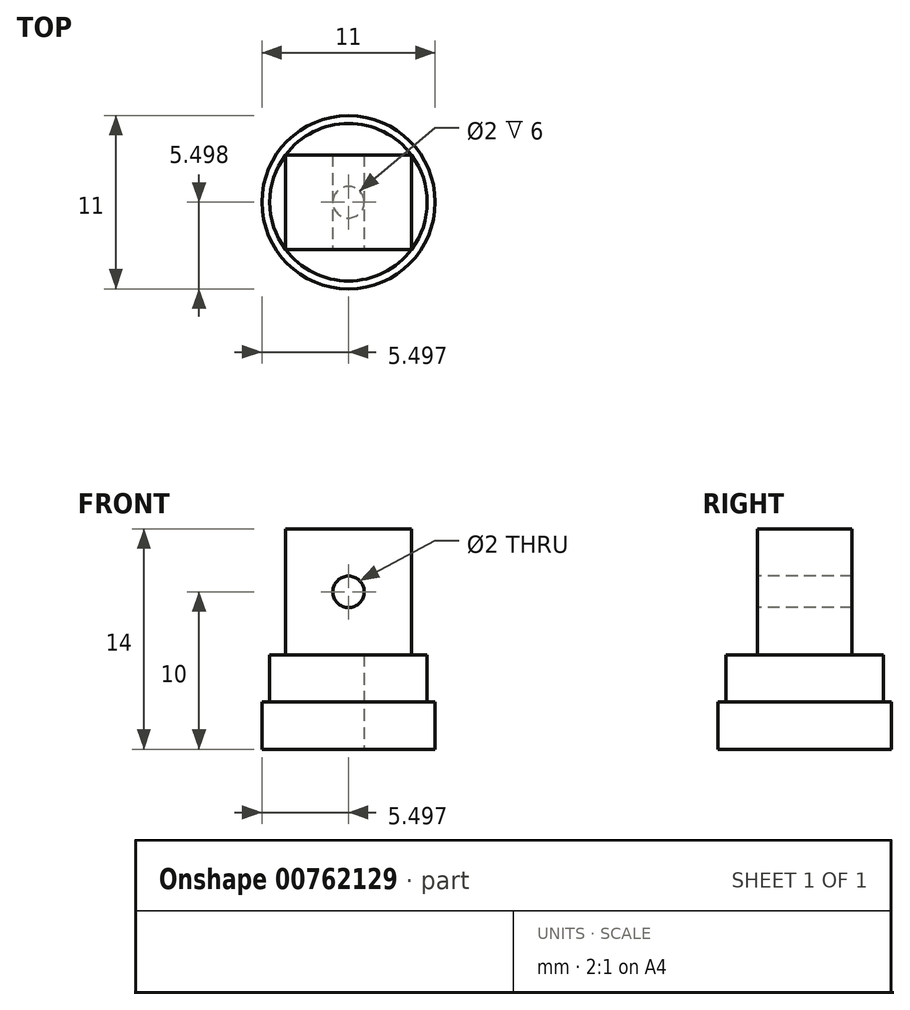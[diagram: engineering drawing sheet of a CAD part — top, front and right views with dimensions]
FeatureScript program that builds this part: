
annotation { "Feature Type Name" : "Feature", "Feature Type Description" : "" }
export const myFeature = defineFeature(function(context is Context, id is Id, definition is map)
    precondition{}
    {
        {
            var Q0;
            Q0=qCreatedBy(makeId("Top.planeOp"),FACE);
            var sketch = newSketch(context, id + "F0", { "sketchPlane" : qUnion([Q0])});
            skCircle(sketch, "E0", {"center": v(-27.4, 27.86) * mm, "radius": 5.5 * mm});
            skCircle(sketch, "E1", {"center": v(-27.4, 27.86) * mm, "radius": 1 * mm});
            skSolve(sketch);
        }
        {
            var Q0;
            Q0=makeQuery(id+"F0.imprint","IMPRINT",FACE,{"disambiguationData":[TD([[makeQuery(id+"F0.imprint","IMPRINT",EDGE,{"derivedFrom":sQuery(id+"F0.wireOp",EDGE,"E0")}),1.0]])]});
            extrude(context, id + "F1", {"entities" : qUnion([Q0]), "depth" : 3 * mm, "offsetDistance" : 25 * mm});
        }
        {
            var Q0;
            Q0=makeQuery(id+"F1.opExtrude","CAP_FACE",FACE,{"disambiguationData":[OSD([sQuery(id+"F0.wireOp",EDGE,"E0")])],"isStart":false});
            var sketch = newSketch(context, id + "F2", { "sketchPlane" : qUnion([Q0])});
            skCircle(sketch, "E2", {"center": v(-27.4, 27.86) * mm, "radius": 5 * mm});
            skSolve(sketch);
        }
        {
            var Q0;
            Q0=makeQuery(id+"F2.imprint","IMPRINT",FACE,{"disambiguationData":[TD([[makeQuery(id+"F2.imprint","IMPRINT",EDGE,{"derivedFrom":sQuery(id+"F2.wireOp",EDGE,"E2")}),1.0]])]});
            extrude(context, id + "F3", {"entities" : qUnion([Q0]), "operationType" : NewBodyOperationType.ADD, "depth" : 3 * mm, "offsetDistance" : 25 * mm});
        }
        {
            var Q0;
            Q0=makeQuery(id+"F3.opExtrude","CAP_FACE",FACE,{"disambiguationData":[OSD([sQuery(id+"F0.wireOp",EDGE,"E1"),sQuery(id+"F2.wireOp",EDGE,"E2")])],"isStart":false});
            var sketch = newSketch(context, id + "F4", { "sketchPlane" : qUnion([Q0])});
            skLineSegment(sketch, "E3", {"start": v(-31.4, 30.86) * mm, "end": v(-23.4, 30.86) * mm});
            skLineSegment(sketch, "E4", {"start": v(-23.4, 30.86) * mm, "end": v(-23.4, 24.86) * mm});
            skLineSegment(sketch, "E5", {"start": v(-23.4, 24.86) * mm, "end": v(-31.4, 24.86) * mm});
            skLineSegment(sketch, "E6", {"start": v(-31.4, 24.86) * mm, "end": v(-31.4, 30.86) * mm});
            skSolve(sketch);
        }
        {
            var Q0;
            Q0=makeQuery(id+"F4.imprint","IMPRINT",FACE,{"disambiguationData":[TD([[makeQuery(id+"F4.imprint","IMPRINT",EDGE,{"derivedFrom":sQuery(id+"F4.wireOp",EDGE,"E3")}),-1.0]])]});
            var Q1;
            Q1=makeQuery(id+"F4.imprint","IMPRINT",FACE,{"disambiguationData":[TD([[makeQuery(id+"F4.imprint","IMPRINT",EDGE,{"derivedFrom":makeQuery(id+"F3.opExtrude","CAP_EDGE",EDGE,{"disambiguationData":[OSD([sQuery(id+"F0.wireOp",EDGE,"E1")])],"isStart":false})}),1.0]])]});
            extrude(context, id + "F5", {"entities" : qUnion([Q0, Q1]), "operationType" : NewBodyOperationType.ADD, "depth" : 8 * mm, "offsetDistance" : 25 * mm});
        }
        {
            var Q0;
            Q0=makeQuery(id+"F5.opExtrude","SWEPT_FACE",FACE,{"disambiguationData":[OSD([sQuery(id+"F4.wireOp",EDGE,"E5")])]});
            var sketch = newSketch(context, id + "F6", { "sketchPlane" : qUnion([Q0])});
            skCircle(sketch, "E7", {"center": v(-27.4, 10) * mm, "radius": 1 * mm});
            skPoint(sketch, "E7.centerSnap0", {"position": v(-27.4, 14) * mm});
            skSolve(sketch);
        }
        {
            var Q0;
            Q0=makeQuery(id+"F6.imprint","IMPRINT",FACE,{"disambiguationData":[TD([[makeQuery(id+"F6.imprint","IMPRINT",EDGE,{"derivedFrom":sQuery(id+"F6.wireOp",EDGE,"E7")}),1.0]])]});
            extrude(context, id + "F7", {"entities" : qUnion([Q0]), "operationType" : NewBodyOperationType.REMOVE, "oppositeDirection" : true, "depth" : 25 * mm, "offsetDistance" : 25 * mm});
        }
    });
